# Revit family: d0090604_REVIT-IS(D) 60-80 Prefix
name_source: partatom
category: Mechanical Equipment
revit_build: Autodesk Revit 2017 (Build: 20190507_1515(x64)
units: mm (PartAtom-declared; Revit-internal decimal feet)

## family parameters
Always vertical = Yes
Cut with Voids When Loaded = No
Part Type = Normal
Room Calculation Point = No
Round Connector Dimension = Use Radius
Shared = No
Work Plane-Based = No

## types (4) — shared parameters
A = 17 3/16"
Assembly Code = D3040400
Cold Inlet Flange = 3"
Cold Inlet Radius = 1 1/2"
Control Panel Extension = 22"
Current = 2 A
Description = PVI QuickDraw - Semi-Instantaneous Hot Water Heater
Disclaimer = This rendering is for building modeling purposes only. Submittal/catalog is still the contract document. PVI reserves the right to change design and specification without notice.
Drain Extension = 18 1/2"
Drain Radius = 1/2"
Drain Valve NPT = 1"
Dual Manifold Offset = 5 7/8"
Height To Cold Inlet = 27 5/16"
Height To Drain = 37 3/4"
Height To Relief = 93 5/16"
Manufacturer = PVI Industries, LLC
Relief Extension = 16"
Relief Radius = 3/8"
Relief Valve NPT = 3/4"
Skid Height = 33 3/8"
Skid Runner Height = 1 3/8"
Steam Inlet High Input NPT (60 Prefix & up) = 2 1/2"
Steam Inlet High Input Radius = 1 1/4"
Steam Inlet Length X = 31 9/16"
Steam Inlet Length Y = 9 3/8"
Steam Inlet NPT = 2 1/2"
Steam Inlet Offset 2 = No
Steam Inlet Offset X = 5 7/8"
Steam Inlet Radius = 1 1/4"
Steam Manifold Crossover Location = 28 7/16"
Steam Outlet Extension = 14 1/8"
Steam Pressure = 15.00 psi
Steam Radius Inlet = 2 1/2"
U Tube Length = 13 5/8"
URL = www.pvi.com
Unit Radius = 15"

## per-type parameters (varying)
| type | Condensate Outlet NPT | Hot Outlet NPT | Hot Outlet Radius | Recovery Rate 40F to 140F | Relief Valve Location | Steam Flow lb/hr | Steam Inlet Connection Offset Y | Steam Outlet Connection Offset Y | Steam Outlet Radius | U Tube Radius | Unit Height | Weight |
| 80 L 5A-ISD | 4" | 3" | 1 1/2" | 59 GPM | 81 5/16" | 3070 | 2 15/16" | 2 15/16" | 2" | 7 5/16" | 95" | 1030.00 lb |
| 80 L 5A-IS | 4" | 3" | 1 1/2" | 59 GPM | 69 5/16" | 3070 | 2 15/16" | 2 15/16" | 2" | 7 5/16" | 83" | 790.00 lb |
| 60 L 5A-ISD | 3" | 2" | 1" | 45 GPM | 69 5/16" | 2300 | 2 15/16" | 2 15/16" | 1 1/2" | 7 5/16" | 83" | 910.00 lb |
| 60 L 5A-IS | 3" | 2" | 1" | 45 GPM | 81 5/16" | 2300 | 2 1/2" | 2 1/2" | 1 1/2" | 6 1/4" | 95" | 820.00 lb |

note: column(s) folded — value = type name in every type: Model

## geometry (parser evidence)
native form markers: Sweep x2
no freeform markers — native parametric forms only
